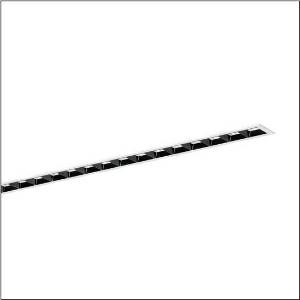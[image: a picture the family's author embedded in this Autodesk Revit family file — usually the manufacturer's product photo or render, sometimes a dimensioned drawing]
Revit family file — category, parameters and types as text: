
# Revit family: silica_21_51mx11dc4awb
name_source: partatom
category: Lighting Fixtures
units: mm (PartAtom-declared; Revit-internal decimal feet)

## family parameters
Cut with Voids When Loaded = No
Host = Face
Light Source = No
Part Type = Normal
Room Calculation Point = No
Round Connector Dimension = Use Diameter
Shared = No

## types (1)
- --- (1 x LED, 10800 lm, 64.8 W, 4000K)
    Apparent Load = 65 VA
    CIE Flux Codes = 87 99 100 100 100
    Color Rendering = 80
    Color Temperature = 4000K
    Default Elevation = 1800 mm
    Description = Silica 21, office luminaire, primary light control with darklight reflector, of PMMA, black, CAT 2 (L<= 3000cd/m²), light emission: direct distribution, primary light characteristic: symmetric, installation type: recessed, LED, rated luminous flux: 10.800lm, luminous efficacy: 167lm/W, light colour: 840, colour temperature: 4000K, control gear: DALI 2, with terminal, 3+2-pole, max. 2.5mm², mains connection: 220..240V, AC, 50/60Hz, rated input power: 64.8W, luminaire housing, of aluminium, traffic white (RAL 9016), length: 3.028mm, width: 79mm, height: 53mm, protection rating (complete): IP20, insulation class (complete): insulation class I (protective earthing), certification: CE, ENEC, VDE, permissible operating ambient temperature: 0..+35°C, standard: EN 50419, packaging unit: 1 piece
    Height = 0 mm  [stored 0 ft]
    Lamp = 1 x LED
    Lamp Light Flux = 10800 lm
    Lamp Power = 64.8 W
    Lamp count = 1
    Length = 3027 mm
    Luminous efficacy = 167 lm/W
    Manufacturer = Siteco
    ModVariant = No
    Model = 51MX11DC4AWB
    Mounting Place = Ceiling
    Mounting Type = Recessed
    Number of Poles = 1
    OnlyDefault = Yes
    Power Factor = 1
    Product Name = Silica 21
    Product group = office luminaire | ceiling recessed
    ProductGroupID = 400
    Protection Class = Protection class I
    Protection Degree = IP 20
    RLX_Detail_Level = 1
    RLX_Emergency_Light_Flux = 0 lm
    RLX_Emergency_Type = 0
    RLX_Emergency_Type_DB = No
    RlxData = <blob elided: 63209 chars, md5=14a71567>
    Socket = socket
    Standby Power = 0 W
    System Light Flux = 10800 lm
    System Power = 65 W
    Type Comments = factory setting: luminous flux: 100 % | dim-lin: 254 | 367 mA
    Type Image = l_1335880.jpg
    URL = http://relux.com
    VarID = @adj_123537
    Voltage = 0 V
    Weight = 0.00 kg
    Width = 79 mm

note: [stored X ft] marks values corroborated as IEEE doubles in the binary element streams (Revit-internal decimal feet)

## geometry (parser evidence)
native form markers: Blend x4, Sweep x11
no freeform markers — native parametric forms only
